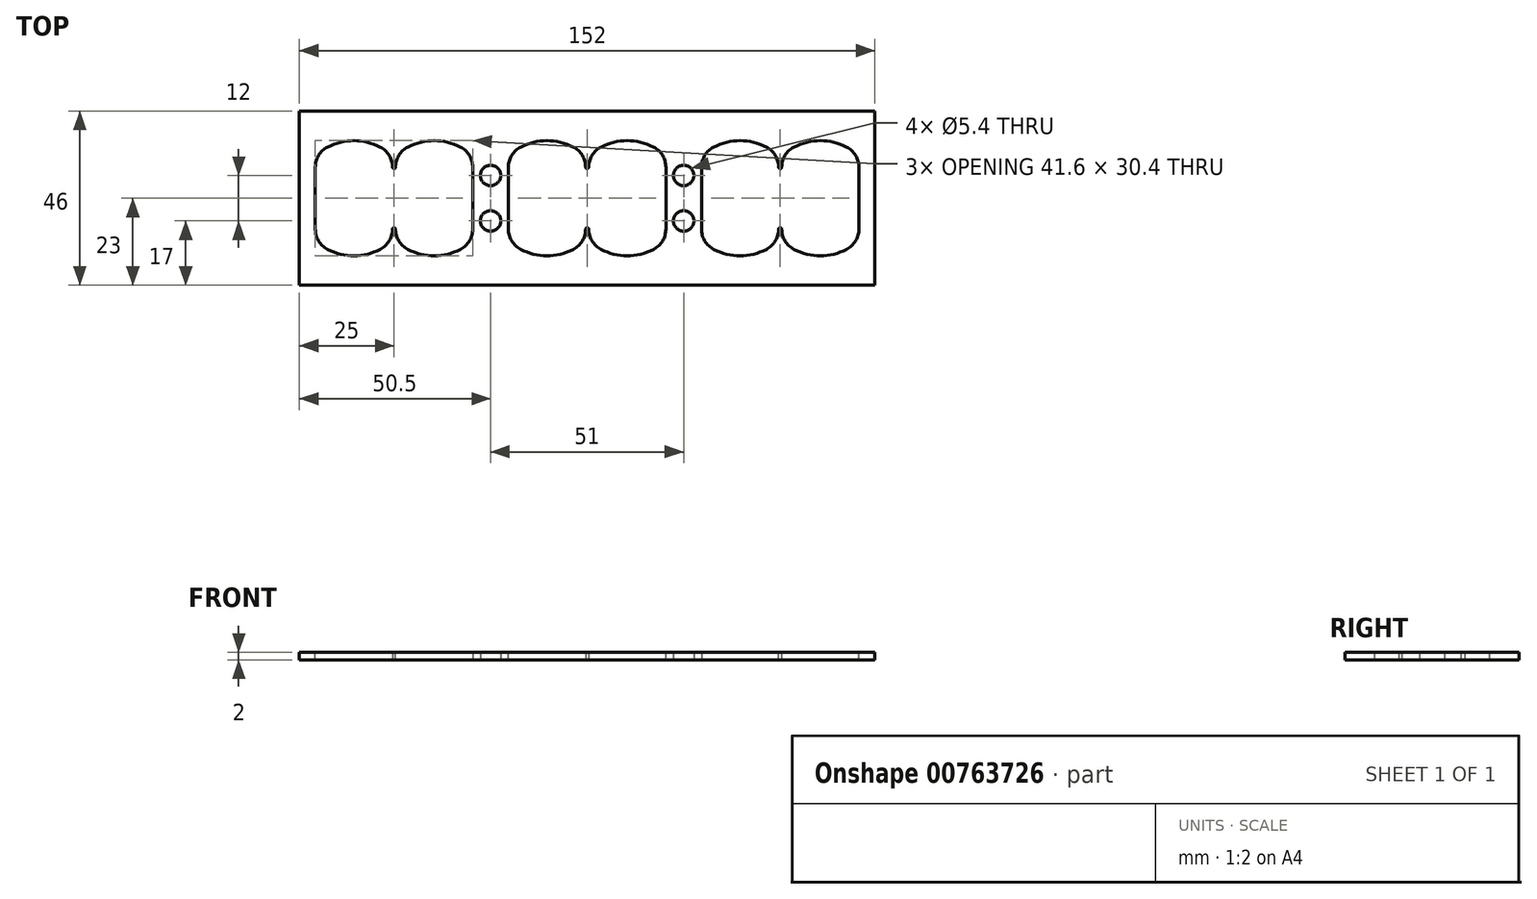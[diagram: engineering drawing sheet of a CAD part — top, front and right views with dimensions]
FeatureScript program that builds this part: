
annotation { "Feature Type Name" : "Feature", "Feature Type Description" : "" }
export const myFeature = defineFeature(function(context is Context, id is Id, definition is map)
    precondition{}
    {
        {
            var Q0;
            Q0=qCreatedBy(makeId("Top.planeOp"),FACE);
            var sketch = newSketch(context, id + "F0", { "sketchPlane" : qUnion([Q0])});
            skLineSegment(sketch, "E0.bottom", {"start": v(-71.8, 15.2) * mm, "end": v(-51.4, 15.2) * mm});
            skLineSegment(sketch, "E0.top", {"start": v(-71.8, -15.2) * mm, "end": v(-51.4, -15.2) * mm});
            skLineSegment(sketch, "E0.left", {"start": v(-71.8, 15.2) * mm, "end": v(-71.8, -15.2) * mm});
            skLineSegment(sketch, "E0.right", {"start": v(-51.4, 15.2) * mm, "end": v(-51.4, -15.2) * mm});
            skLineSegment(sketch, "E1.bottom", {"start": v(-50.6, 15.2) * mm, "end": v(-30.2, 15.2) * mm});
            skLineSegment(sketch, "E1.top", {"start": v(-50.6, -15.2) * mm, "end": v(-30.2, -15.2) * mm});
            skLineSegment(sketch, "E1.left", {"start": v(-50.6, 15.2) * mm, "end": v(-50.6, -15.2) * mm});
            skLineSegment(sketch, "E1.right", {"start": v(-30.2, 15.2) * mm, "end": v(-30.2, -15.2) * mm});
            skLineSegment(sketch, "E2.bottom", {"start": v(-0.4, 15.2) * mm, "end": v(-20.8, 15.2) * mm});
            skLineSegment(sketch, "E2.top", {"start": v(-0.4, -15.2) * mm, "end": v(-20.8, -15.2) * mm});
            skLineSegment(sketch, "E2.left", {"start": v(-0.4, 15.2) * mm, "end": v(-0.4, -15.2) * mm});
            skLineSegment(sketch, "E2.right", {"start": v(-20.8, 15.2) * mm, "end": v(-20.8, -15.2) * mm});
            skCircle(sketch, "E3", {"center": v(-25.5, 6) * mm, "radius": 2.7 * mm});
            skLineSegment(sketch, "E4", {"start": v(-30.2, 0) * mm, "end": v(-20.8, 0) * mm, "construction": true});
            skPoint(sketch, "E5", {"position": v(-25.5, 0) * mm});
            skCircle(sketch, "E6.MirrorC", {"center": v(-25.5, -6) * mm, "radius": 2.7 * mm});
            skLineSegment(sketch, "E7.bottom", {"start": v(-76, 23) * mm, "end": v(0, 23) * mm});
            skLineSegment(sketch, "E7.top", {"start": v(-76, -23) * mm, "end": v(0, -23) * mm});
            skLineSegment(sketch, "E7.left", {"start": v(-76, 23) * mm, "end": v(-76, -23) * mm});
            skLineSegment(sketch, "E7.right", {"start": v(0, 23) * mm, "end": v(0, -23) * mm});
            skPoint(sketch, "E8", {"position": v(0, 0) * mm});
            skLineSegment(sketch, "E9.0", {"start": v(-78.2, 25.2) * mm, "end": v(0, 25.2) * mm});
            skLineSegment(sketch, "E9.1", {"start": v(-78.2, 25.2) * mm, "end": v(-78.2, -25.2) * mm});
            skLineSegment(sketch, "E9.2", {"start": v(-78.2, -25.2) * mm, "end": v(0, -25.2) * mm});
            skLineSegment(sketch, "E10", {"start": v(0, 23) * mm, "end": v(0, 25.2) * mm});
            skLineSegment(sketch, "E11", {"start": v(0, -23) * mm, "end": v(0, -25.2) * mm});
            skArc(sketch, "E12", {"start": v(-71.8, -11.27) * mm, "mid": v(-61.6, -15.2) * mm, "end": v(-51.4, -11.27) * mm});
            skPoint(sketch, "E12.centerSnap0", {"position": v(-71.8, 0) * mm});
            skPoint(sketch, "E12.centerSnap1", {"position": v(-61.6, 15.2) * mm});
            skArc(sketch, "E13.trimOffspring", {"start": v(-51.4, 11.27) * mm, "mid": v(-61.6, 15.2) * mm, "end": v(-71.8, 11.27) * mm});
            skPoint(sketch, "E14.centerSnap0", {"position": v(-40.4, 15.2) * mm});
            skArc(sketch, "E15", {"start": v(-20.8, -11.27) * mm, "mid": v(-10.6, -15.2) * mm, "end": v(-0.4, -11.27) * mm});
            skPoint(sketch, "E15.centerSnap0", {"position": v(-10.6, 15.2) * mm});
            skArc(sketch, "E16.trimOffspring", {"start": v(-0.4, 11.27) * mm, "mid": v(-10.6, 15.2) * mm, "end": v(-20.8, 11.27) * mm});
            skArc(sketch, "E17", {"start": v(-30.2, 11.27) * mm, "mid": v(-40.4, 15.2) * mm, "end": v(-50.6, 11.27) * mm});
            skPoint(sketch, "E17.centerSnap0", {"position": v(-50.6, 0) * mm});
            skArc(sketch, "E18.trimOffspring", {"start": v(-50.6, -11.27) * mm, "mid": v(-40.4, -15.2) * mm, "end": v(-30.2, -11.27) * mm});
            skLineSegment(sketch, "E19", {"start": v(-51.4, 11.27) * mm, "end": v(-52.08, 10.95) * mm, "construction": true});
            skLineSegment(sketch, "E20", {"start": v(-51.4, 11.27) * mm, "end": v(-50.6, 11.27) * mm, "construction": true});
            skLineSegment(sketch, "E21", {"start": v(-51, 11.27) * mm, "end": v(-51, 10.95) * mm, "construction": true});
            skLineSegment(sketch, "E22.MirrorCS", {"start": v(-50.6, 11.27) * mm, "end": v(-49.92, 10.95) * mm, "construction": true});
            skLineSegment(sketch, "E23.MirrorCS", {"start": v(-50.6, -11.27) * mm, "end": v(-49.92, -10.95) * mm, "construction": true});
            skLineSegment(sketch, "E24.MirrorCS", {"start": v(-51.4, -11.27) * mm, "end": v(-52.08, -10.95) * mm, "construction": true});
            skLineSegment(sketch, "E25", {"start": v(-25.5, 0) * mm, "end": v(-25.5, -1.23) * mm, "construction": true});
            skLineSegment(sketch, "E26.MirrorCS", {"start": v(-0.4, 11.27) * mm, "end": v(-1.08, 10.95) * mm, "construction": true});
            skLineSegment(sketch, "E27.MirrorCS", {"start": v(-0.4, -11.27) * mm, "end": v(-1.08, -10.95) * mm, "construction": true});
            skPoint(sketch, "E28", {"position": v(-52.08, 10.95) * mm});
            skPoint(sketch, "E29", {"position": v(-49.92, 10.95) * mm});
            skPoint(sketch, "E30", {"position": v(-52.08, -10.95) * mm});
            skPoint(sketch, "E31", {"position": v(-49.92, -10.95) * mm});
            skPoint(sketch, "E32", {"position": v(-1.08, -10.95) * mm});
            skPoint(sketch, "E33", {"position": v(-1.08, 10.95) * mm});
            skSolve(sketch);
        }
        {
            var Q0;
            Q0=makeQuery(id+"F0.imprint","IMPRINT",FACE,{"disambiguationData":[TD([[makeQuery(id+"F0.imprint","IMPRINT",EDGE,{"derivedFrom":sQuery(id+"F0.wireOp",EDGE,"E0.bottom")}),1.0]])]});
            var Q1;
            {var subQ0=sQuery(id+"F0.wireOp",EDGE,"E0.left");var subQ1=sQuery(id+"F0.wireOp",EDGE,"E0.bottom");var subQ2=makeQuery(id+"F0.imprint","INTERSECT",VERTEX,{"derivedFrom":[subQ1,subQ0]});Q1=makeQuery(id+"F0.imprint","IMPRINT",FACE,{"disambiguationData":[TD([[makeQuery(id+"F0.imprint","IMPRINT",EDGE,{"disambiguationData":[TD([[subQ2,-1.0]])],"derivedFrom":subQ1}),-1.0]])]});}
            var Q2;
            {var subQ0=sQuery(id+"F0.wireOp",EDGE,"E0.right");var subQ1=sQuery(id+"F0.wireOp",EDGE,"E0.bottom");var subQ2=makeQuery(id+"F0.imprint","INTERSECT",VERTEX,{"derivedFrom":[subQ1,subQ0]});Q2=makeQuery(id+"F0.imprint","IMPRINT",FACE,{"disambiguationData":[TD([[makeQuery(id+"F0.imprint","IMPRINT",EDGE,{"disambiguationData":[TD([[subQ2,1.0]])],"derivedFrom":subQ1}),-1.0]])]});}
            var Q3;
            {var subQ0=sQuery(id+"F0.wireOp",EDGE,"E0.right");var subQ1=sQuery(id+"F0.wireOp",EDGE,"E0.top");var subQ2=makeQuery(id+"F0.imprint","INTERSECT",VERTEX,{"derivedFrom":[subQ1,subQ0]});Q3=makeQuery(id+"F0.imprint","IMPRINT",FACE,{"disambiguationData":[TD([[makeQuery(id+"F0.imprint","IMPRINT",EDGE,{"disambiguationData":[TD([[subQ2,1.0]])],"derivedFrom":subQ1}),1.0]])]});}
            var Q4;
            {var subQ0=sQuery(id+"F0.wireOp",EDGE,"E0.left");var subQ1=sQuery(id+"F0.wireOp",EDGE,"E0.top");var subQ2=makeQuery(id+"F0.imprint","INTERSECT",VERTEX,{"derivedFrom":[subQ1,subQ0]});Q4=makeQuery(id+"F0.imprint","IMPRINT",FACE,{"disambiguationData":[TD([[makeQuery(id+"F0.imprint","IMPRINT",EDGE,{"disambiguationData":[TD([[subQ2,-1.0]])],"derivedFrom":subQ1}),1.0]])]});}
            var Q5;
            {var subQ0=sQuery(id+"F0.wireOp",EDGE,"E1.left");var subQ1=sQuery(id+"F0.wireOp",EDGE,"E1.bottom");var subQ2=makeQuery(id+"F0.imprint","INTERSECT",VERTEX,{"derivedFrom":[subQ1,subQ0]});Q5=makeQuery(id+"F0.imprint","IMPRINT",FACE,{"disambiguationData":[TD([[makeQuery(id+"F0.imprint","IMPRINT",EDGE,{"disambiguationData":[TD([[subQ2,-1.0]])],"derivedFrom":subQ1}),-1.0]])]});}
            var Q6;
            {var subQ0=sQuery(id+"F0.wireOp",EDGE,"E1.right");var subQ1=sQuery(id+"F0.wireOp",EDGE,"E1.bottom");var subQ2=makeQuery(id+"F0.imprint","INTERSECT",VERTEX,{"derivedFrom":[subQ1,subQ0]});Q6=makeQuery(id+"F0.imprint","IMPRINT",FACE,{"disambiguationData":[TD([[makeQuery(id+"F0.imprint","IMPRINT",EDGE,{"disambiguationData":[TD([[subQ2,1.0]])],"derivedFrom":subQ1}),-1.0]])]});}
            var Q7;
            {var subQ0=sQuery(id+"F0.wireOp",EDGE,"E2.right");var subQ1=sQuery(id+"F0.wireOp",EDGE,"E2.bottom");var subQ2=makeQuery(id+"F0.imprint","INTERSECT",VERTEX,{"derivedFrom":[subQ1,subQ0]});Q7=makeQuery(id+"F0.imprint","IMPRINT",FACE,{"disambiguationData":[TD([[makeQuery(id+"F0.imprint","IMPRINT",EDGE,{"disambiguationData":[TD([[subQ2,1.0]])],"derivedFrom":subQ1}),1.0]])]});}
            var Q8;
            {var subQ0=sQuery(id+"F0.wireOp",EDGE,"E2.left");var subQ1=sQuery(id+"F0.wireOp",EDGE,"E2.bottom");var subQ2=makeQuery(id+"F0.imprint","INTERSECT",VERTEX,{"derivedFrom":[subQ1,subQ0]});Q8=makeQuery(id+"F0.imprint","IMPRINT",FACE,{"disambiguationData":[TD([[makeQuery(id+"F0.imprint","IMPRINT",EDGE,{"disambiguationData":[TD([[subQ2,-1.0]])],"derivedFrom":subQ1}),1.0]])]});}
            var Q9;
            {var subQ0=sQuery(id+"F0.wireOp",EDGE,"E2.left");var subQ1=sQuery(id+"F0.wireOp",EDGE,"E2.top");var subQ2=makeQuery(id+"F0.imprint","INTERSECT",VERTEX,{"derivedFrom":[subQ1,subQ0]});Q9=makeQuery(id+"F0.imprint","IMPRINT",FACE,{"disambiguationData":[TD([[makeQuery(id+"F0.imprint","IMPRINT",EDGE,{"disambiguationData":[TD([[subQ2,-1.0]])],"derivedFrom":subQ1}),-1.0]])]});}
            var Q10;
            {var subQ0=sQuery(id+"F0.wireOp",EDGE,"E2.right");var subQ1=sQuery(id+"F0.wireOp",EDGE,"E2.top");var subQ2=makeQuery(id+"F0.imprint","INTERSECT",VERTEX,{"derivedFrom":[subQ1,subQ0]});Q10=makeQuery(id+"F0.imprint","IMPRINT",FACE,{"disambiguationData":[TD([[makeQuery(id+"F0.imprint","IMPRINT",EDGE,{"disambiguationData":[TD([[subQ2,1.0]])],"derivedFrom":subQ1}),-1.0]])]});}
            var Q11;
            {var subQ0=sQuery(id+"F0.wireOp",EDGE,"E1.right");var subQ1=sQuery(id+"F0.wireOp",EDGE,"E1.top");var subQ2=makeQuery(id+"F0.imprint","INTERSECT",VERTEX,{"derivedFrom":[subQ1,subQ0]});Q11=makeQuery(id+"F0.imprint","IMPRINT",FACE,{"disambiguationData":[TD([[makeQuery(id+"F0.imprint","IMPRINT",EDGE,{"disambiguationData":[TD([[subQ2,1.0]])],"derivedFrom":subQ1}),1.0]])]});}
            var Q12;
            {var subQ0=sQuery(id+"F0.wireOp",EDGE,"E1.left");var subQ1=sQuery(id+"F0.wireOp",EDGE,"E1.top");var subQ2=makeQuery(id+"F0.imprint","INTERSECT",VERTEX,{"derivedFrom":[subQ1,subQ0]});Q12=makeQuery(id+"F0.imprint","IMPRINT",FACE,{"disambiguationData":[TD([[makeQuery(id+"F0.imprint","IMPRINT",EDGE,{"disambiguationData":[TD([[subQ2,-1.0]])],"derivedFrom":subQ1}),1.0]])]});}
            extrude(context, id + "F1", {"entities" : qUnion([Q0, Q1, Q2, Q3, Q4, Q5, Q6, Q7, Q8, Q9, Q10, Q11, Q12]), "depth" : 2 * mm, "offsetDistance" : 25 * mm});
        }
        {
            var Q0;
            Q0=makeQuery(id+"F1.opExtrude","SWEPT_EDGE",EDGE,{"disambiguationData":[OSD([sQuery(id+"F0.wireOp",EDGE,"E0.left"),sQuery(id+"F0.wireOp",EDGE,"E13.trimOffspring")])]});
            var Q1;
            Q1=makeQuery(id+"F1.opExtrude","SWEPT_EDGE",EDGE,{"disambiguationData":[OSD([sQuery(id+"F0.wireOp",EDGE,"E0.left"),sQuery(id+"F0.wireOp",EDGE,"E12")])]});
            var Q2;
            Q2=makeQuery(id+"F1.opExtrude","SWEPT_EDGE",EDGE,{"disambiguationData":[OSD([sQuery(id+"F0.wireOp",EDGE,"E0.right"),sQuery(id+"F0.wireOp",EDGE,"E12")])]});
            var Q3;
            Q3=makeQuery(id+"F1.opExtrude","SWEPT_EDGE",EDGE,{"disambiguationData":[OSD([sQuery(id+"F0.wireOp",EDGE,"E0.right"),sQuery(id+"F0.wireOp",EDGE,"E13.trimOffspring")])]});
            var Q4;
            Q4=makeQuery(id+"F1.opExtrude","SWEPT_EDGE",EDGE,{"disambiguationData":[OSD([sQuery(id+"F0.wireOp",EDGE,"E1.left"),sQuery(id+"F0.wireOp",EDGE,"118791d4-9d35-43d1-ba12-05aa415864b6.trimOffspring")])]});
            var Q5;
            Q5=makeQuery(id+"F1.opExtrude","SWEPT_EDGE",EDGE,{"disambiguationData":[OSD([sQuery(id+"F0.wireOp",EDGE,"E1.left"),sQuery(id+"F0.wireOp",EDGE,"E14")])]});
            var Q6;
            Q6=makeQuery(id+"F1.opExtrude","SWEPT_EDGE",EDGE,{"disambiguationData":[OSD([sQuery(id+"F0.wireOp",EDGE,"E2.right"),sQuery(id+"F0.wireOp",EDGE,"E16.trimOffspring")])]});
            var Q7;
            Q7=makeQuery(id+"F1.opExtrude","SWEPT_EDGE",EDGE,{"disambiguationData":[OSD([sQuery(id+"F0.wireOp",EDGE,"E2.right"),sQuery(id+"F0.wireOp",EDGE,"E15")])]});
            var Q8;
            Q8=makeQuery(id+"F1.opExtrude","SWEPT_EDGE",EDGE,{"disambiguationData":[OSD([sQuery(id+"F0.wireOp",EDGE,"E2.left"),sQuery(id+"F0.wireOp",EDGE,"E16.trimOffspring")])]});
            var Q9;
            Q9=makeQuery(id+"F1.opExtrude","SWEPT_EDGE",EDGE,{"disambiguationData":[OSD([sQuery(id+"F0.wireOp",EDGE,"E2.left"),sQuery(id+"F0.wireOp",EDGE,"E15")])]});
            var Q10;
            Q10=makeQuery(id+"F1.opExtrude","SWEPT_EDGE",EDGE,{"disambiguationData":[OSD([sQuery(id+"F0.wireOp",EDGE,"E1.right"),sQuery(id+"F0.wireOp",EDGE,"E14")])]});
            var Q11;
            Q11=makeQuery(id+"F1.opExtrude","SWEPT_EDGE",EDGE,{"disambiguationData":[OSD([sQuery(id+"F0.wireOp",EDGE,"E1.right"),sQuery(id+"F0.wireOp",EDGE,"118791d4-9d35-43d1-ba12-05aa415864b6.trimOffspring")])]});
            fillet(context, id + "F2", {"entities" : qUnion([Q0, Q1, Q2, Q3, Q4, Q5, Q6, Q7, Q8, Q9, Q10, Q11]), "radius" : 6 * mm, "tangentPropagation" : true, "allowEdgeOverflow" : false});
        }
        {
            var Q0;
            Q0=makeQuery(id+"F1.opExtrude","SWEPT_BODY",BODY,{"disambiguationData":[OSD([sQuery(id+"F0.wireOp",EDGE,"E0.left"),sQuery(id+"F0.wireOp",EDGE,"E0.right"),sQuery(id+"F0.wireOp",EDGE,"E1.left"),sQuery(id+"F0.wireOp",EDGE,"E1.right"),sQuery(id+"F0.wireOp",EDGE,"E2.left"),sQuery(id+"F0.wireOp",EDGE,"E2.right"),sQuery(id+"F0.wireOp",EDGE,"E3"),sQuery(id+"F0.wireOp",EDGE,"E6.MirrorC"),sQuery(id+"F0.wireOp",EDGE,"E7.bottom"),sQuery(id+"F0.wireOp",EDGE,"E7.top"),sQuery(id+"F0.wireOp",EDGE,"E7.left"),sQuery(id+"F0.wireOp",EDGE,"E7.right"),sQuery(id+"F0.wireOp",EDGE,"E12"),sQuery(id+"F0.wireOp",EDGE,"E13.trimOffspring"),sQuery(id+"F0.wireOp",EDGE,"E15"),sQuery(id+"F0.wireOp",EDGE,"E16.trimOffspring"),sQuery(id+"F0.wireOp",EDGE,"E17"),sQuery(id+"F0.wireOp",EDGE,"E18.trimOffspring")])]});
            var Q1;
            Q1=makeQuery(id+"F1.opExtrude","SWEPT_FACE",FACE,{"disambiguationData":[OSD([sQuery(id+"F0.wireOp",EDGE,"E7.right")])]});
            mirror(context, id + "F3", {"operationType" : NewBodyOperationType.ADD, "entities" : qUnion([Q0]), "mirrorPlane" : qUnion([Q1])});
        }
        {
            var Q0;
            {var subQ0=makeQuery(id+"F1.opExtrude","CAP_FACE",FACE,{"disambiguationData":[OSD([sQuery(id+"F0.wireOp",EDGE,"E0.left"),sQuery(id+"F0.wireOp",EDGE,"E0.right"),sQuery(id+"F0.wireOp",EDGE,"E1.left"),sQuery(id+"F0.wireOp",EDGE,"E1.right"),sQuery(id+"F0.wireOp",EDGE,"E2.left"),sQuery(id+"F0.wireOp",EDGE,"E2.right"),sQuery(id+"F0.wireOp",EDGE,"E3"),sQuery(id+"F0.wireOp",EDGE,"E6.MirrorC"),sQuery(id+"F0.wireOp",EDGE,"E7.bottom"),sQuery(id+"F0.wireOp",EDGE,"E7.top"),sQuery(id+"F0.wireOp",EDGE,"E7.left"),sQuery(id+"F0.wireOp",EDGE,"E7.right"),sQuery(id+"F0.wireOp",EDGE,"E12"),sQuery(id+"F0.wireOp",EDGE,"E13.trimOffspring"),sQuery(id+"F0.wireOp",EDGE,"E15"),sQuery(id+"F0.wireOp",EDGE,"E16.trimOffspring"),sQuery(id+"F0.wireOp",EDGE,"E17"),sQuery(id+"F0.wireOp",EDGE,"E18.trimOffspring")])],"isStart":false});Q0=makeQuery(id+"F3.boolean.opBoolean","MERGE",FACE,{"derivedFrom":[subQ0,makeQuery(id+"F3.opPattern","COPY",FACE,{"derivedFrom":subQ0,"instanceName":"1"})]});}
            var sketch = newSketch(context, id + "F4", { "sketchPlane" : qUnion([Q0])});
            skArc(sketch, "E34", {"start": v(-51.4, 8.19) * mm, "mid": v(-51, 7.79) * mm, "end": v(-50.6, 8.19) * mm});
            skArc(sketch, "E35.MirrorCS", {"start": v(-51.4, -8.19) * mm, "mid": v(-51, -7.79) * mm, "end": v(-50.6, -8.19) * mm});
            skArc(sketch, "E36", {"start": v(-0.4, 8.19) * mm, "mid": v(0, 7.79) * mm, "end": v(0.4, 8.19) * mm});
            skArc(sketch, "E37", {"start": v(50.6, 8.19) * mm, "mid": v(51, 7.79) * mm, "end": v(51.4, 8.19) * mm});
            skArc(sketch, "E38.MirrorCS", {"start": v(-0.4, -8.19) * mm, "mid": v(0, -7.79) * mm, "end": v(0.4, -8.19) * mm});
            skArc(sketch, "E39.MirrorCS", {"start": v(50.6, -8.19) * mm, "mid": v(51, -7.79) * mm, "end": v(51.4, -8.19) * mm});
            skSolve(sketch);
        }
        {
            var Q0;
            Q0=makeQuery(id+"F4.imprint","IMPRINT",FACE,{"disambiguationData":[TD([[makeQuery(id+"F4.imprint","IMPRINT",EDGE,{"derivedFrom":sQuery(id+"F4.wireOp",EDGE,"E36")}),-1.0]])]});
            var Q1;
            Q1=makeQuery(id+"F4.imprint","IMPRINT",FACE,{"disambiguationData":[TD([[makeQuery(id+"F4.imprint","IMPRINT",EDGE,{"derivedFrom":sQuery(id+"F4.wireOp",EDGE,"E37")}),-1.0]])]});
            var Q2;
            Q2=makeQuery(id+"F4.imprint","IMPRINT",FACE,{"disambiguationData":[TD([[makeQuery(id+"F4.imprint","IMPRINT",EDGE,{"derivedFrom":sQuery(id+"F4.wireOp",EDGE,"E34")}),-1.0]])]});
            extrude(context, id + "F5", {"entities" : qUnion([Q0, Q1, Q2]), "operationType" : NewBodyOperationType.REMOVE, "oppositeDirection" : true, "depth" : 25 * mm, "offsetDistance" : 25 * mm});
        }
    });
